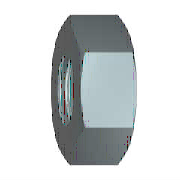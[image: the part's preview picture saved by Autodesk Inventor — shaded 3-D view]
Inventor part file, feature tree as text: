
AUTODESK INVENTOR PART (.ipt)
format: ipt  version: 2015 SP1 (Build 190203100, 203)  size: 171,008 bytes
history: native  units: mm (DEFAULTED — no unit token found)
features: sketch x3, chamfer x1, hole x1, other x1, plane x1
ambient origin geometry x7: Origin, YZ Plane, XZ Plane, X Axis, Y Axis, Z Axis, Center Point
bodies: Solid1 (feature_tree), Body (feature_tree)
feature tree (7):
  chamfer  "Chamfer1"  Angle=30.0deg  [1 undecoded]
  hole  "Thread"  [1 undecoded]
  other  "Work Axis1"
  plane  "Work Plane1"
  sketch  "Sketch1"  dims[d0=6.350853mm]
  sketch  "Sketch2"  dims[d1=2.4mm]
  sketch  "Sketch3"  dims[d2=0.0mm d3=30.0deg d4=30.0deg d5=5.5mm d6=5.5mm d7=90.0deg d25=2.459mm d26=6.0mm d27=4.0mm d28=2.0mm d29=14.3117mm d30=8.0mm d31=20.594885mm d8=0.270633mm d9=30.0deg d10=0.270633mm d11=30.0deg d13=0.0mm d14=0.0mm d39=0.0mm d40=0.270633mm d41=0.270633mm d42=0.0mm]
note: 2 required parameter values undecoded (feature->parameter linkage not recoverable at this tier; creation-order binding heuristic only, values carry confidence <= 0.55)
